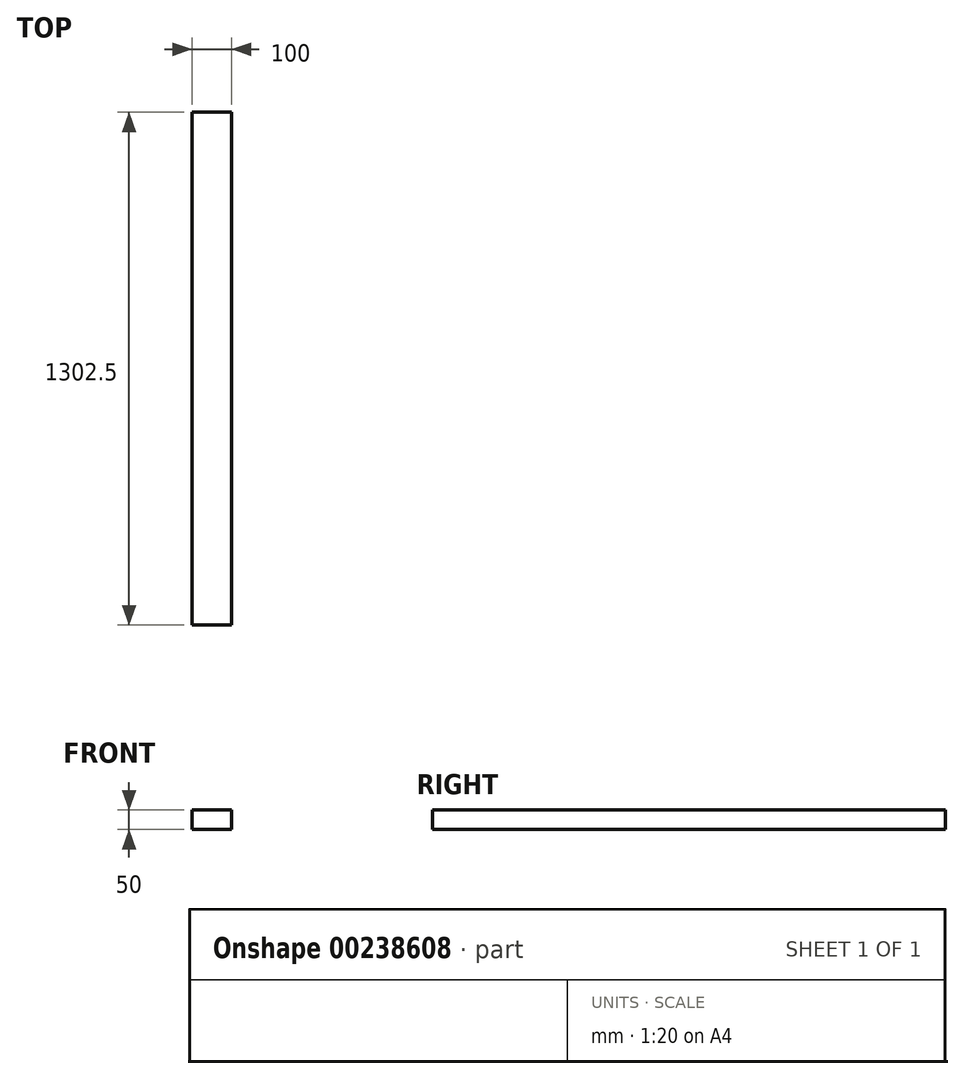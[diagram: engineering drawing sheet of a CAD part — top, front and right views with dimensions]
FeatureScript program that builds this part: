
annotation { "Feature Type Name" : "Feature", "Feature Type Description" : "" }
export const myFeature = defineFeature(function(context is Context, id is Id, definition is map)
    precondition{}
    {
        {
            var Q0;
            Q0=qCreatedBy(makeId("Front.planeOp"),FACE);
            var sketch = newSketch(context, id + "F0", { "sketchPlane" : qUnion([Q0])});
            skLineSegment(sketch, "E0.bottom", {"start": v(50, -25) * mm, "end": v(-50, -25) * mm});
            skLineSegment(sketch, "E0.top", {"start": v(50, 25) * mm, "end": v(-50, 25) * mm});
            skLineSegment(sketch, "E0.left", {"start": v(50, -25) * mm, "end": v(50, 25) * mm});
            skLineSegment(sketch, "E0.right", {"start": v(-50, -25) * mm, "end": v(-50, 25) * mm});
            skPoint(sketch, "E0.middle", {"position": v(0, 0) * mm});
            skSolve(sketch);
        }
        {
            var Q0;
            Q0=makeQuery(id+"F0.imprint","IMPRINT",FACE,{"disambiguationData":[TD([[makeQuery(id+"F0.imprint","IMPRINT",EDGE,{"derivedFrom":sQuery(id+"F0.wireOp",EDGE,"E0.bottom")}),-1.0]])]});
            extrude(context, id + "F1", {"entities" : qUnion([Q0]), "depth" : 1302.5 * mm});
        }
    });
